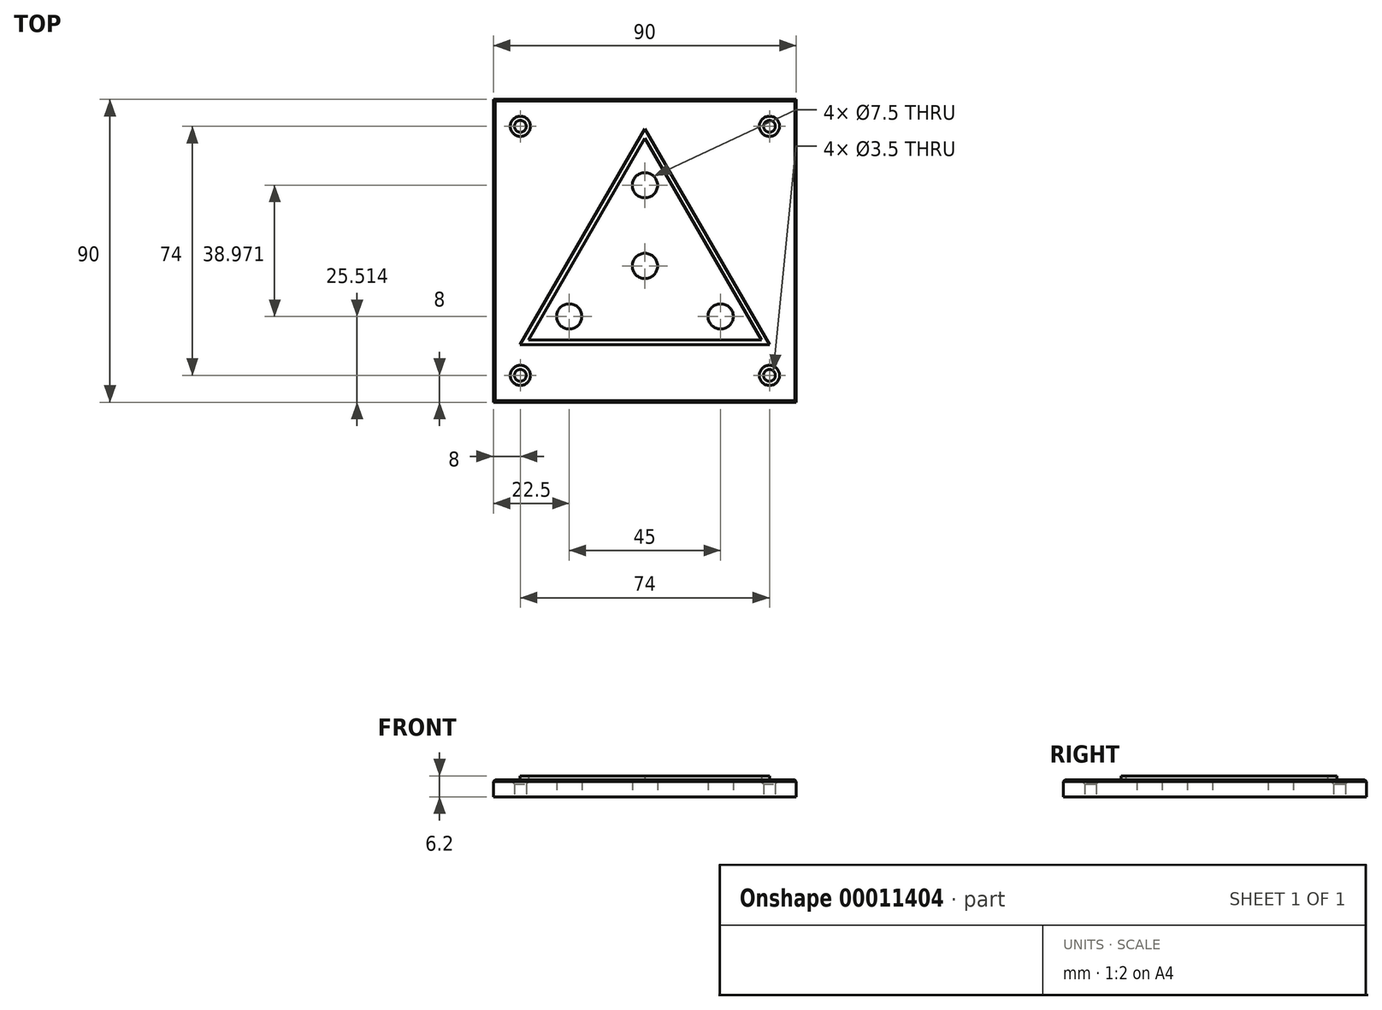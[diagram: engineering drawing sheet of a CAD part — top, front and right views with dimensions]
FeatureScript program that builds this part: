
annotation { "Feature Type Name" : "Feature", "Feature Type Description" : "" }
export const myFeature = defineFeature(function(context is Context, id is Id, definition is map)
    precondition{}
    {
        {
            var Q0;
            Q0=qCreatedBy(makeId("Top.planeOp"),FACE);
            var sketch = newSketch(context, id + "F0", { "sketchPlane" : qUnion([Q0])});
            skLineSegment(sketch, "E0.bottom", {"start": v(-45, 45) * mm, "end": v(45, 45) * mm});
            skLineSegment(sketch, "E0.top", {"start": v(-45, -45) * mm, "end": v(45, -45) * mm});
            skLineSegment(sketch, "E0.left", {"start": v(-45, 45) * mm, "end": v(-45, -45) * mm});
            skLineSegment(sketch, "E0.right", {"start": v(45, 45) * mm, "end": v(45, -45) * mm});
            skLineSegment(sketch, "E1", {"start": v(-45, -45) * mm, "end": v(45, 45) * mm, "construction": true});
            skPoint(sketch, "E2", {"position": v(0, 19.49) * mm});
            skPoint(sketch, "E3", {"position": v(-22.5, -19.49) * mm});
            skPoint(sketch, "E4", {"position": v(22.5, -19.49) * mm});
            skPoint(sketch, "E5", {"position": v(0, -4.49) * mm});
            skLineSegment(sketch, "E6", {"start": v(0, 19.49) * mm, "end": v(-22.5, -19.49) * mm, "construction": true});
            skLineSegment(sketch, "E7", {"start": v(22.5, -19.49) * mm, "end": v(-22.5, -19.49) * mm, "construction": true});
            skLineSegment(sketch, "E8", {"start": v(0, 19.49) * mm, "end": v(22.5, -19.49) * mm, "construction": true});
            skLineSegment(sketch, "E9", {"start": v(0, 19.49) * mm, "end": v(0, -19.49) * mm, "construction": true});
            skLineSegment(sketch, "E10", {"start": v(0, 19.49) * mm, "end": v(0, 45) * mm, "construction": true});
            skLineSegment(sketch, "E11", {"start": v(0, -19.49) * mm, "end": v(0, -45) * mm, "construction": true});
            skSolve(sketch);
        }
        {
            var Q0;
            Q0 = qSketchRegion(id + "F0", true);
            extrude(context, id + "F1", {"entities" : qUnion([Q0]), "depth" : 5 * mm});
        }
        {
            var Q0;
            Q0=qCreatedBy(makeId("Top.planeOp"),FACE);
            var sketch = newSketch(context, id + "F2", { "sketchPlane" : qUnion([Q0])});
            skPoint(sketch, "E12.0", {"position": v(0, 19.49) * mm});
            skPoint(sketch, "E12.1", {"position": v(-22.5, -19.49) * mm});
            skPoint(sketch, "E12.2", {"position": v(22.5, -19.49) * mm});
            skPoint(sketch, "E12.3", {"position": v(0, -4.49) * mm});
            skCircle(sketch, "E13", {"center": v(0, 19.49) * mm, "radius": 3.75 * mm});
            skCircle(sketch, "E14", {"center": v(0, -4.49) * mm, "radius": 3.75 * mm});
            skCircle(sketch, "E15", {"center": v(-22.5, -19.49) * mm, "radius": 3.75 * mm});
            skCircle(sketch, "E16", {"center": v(22.5, -19.49) * mm, "radius": 3.75 * mm});
            skSolve(sketch);
        }
        {
            var Q0;
            Q0 = qSketchRegion(id + "F2", true);
            extrude(context, id + "F3", {"entities" : qUnion([Q0]), "operationType" : NewBodyOperationType.REMOVE, "endBound" : BoundingType.THROUGH_ALL, "depth" : 1 * mm});
        }
        {
            var Q0;
            Q0=makeQuery(id+"F1.opExtrude","CAP_FACE",FACE,{"disambiguationData":[OSD([sQuery(id+"F0.wireOp",EDGE,"E0.bottom"),sQuery(id+"F0.wireOp",EDGE,"E0.top"),sQuery(id+"F0.wireOp",EDGE,"E0.left"),sQuery(id+"F0.wireOp",EDGE,"E0.right")])],"isStart":false});
            var sketch = newSketch(context, id + "F4", { "sketchPlane" : qUnion([Q0])});
            skLineSegment(sketch, "E17", {"start": v(0, 33.49) * mm, "end": v(-34.62, -26.49) * mm});
            skLineSegment(sketch, "E18", {"start": v(-34.62, -26.49) * mm, "end": v(34.62, -26.49) * mm});
            skLineSegment(sketch, "E19", {"start": v(34.62, -26.49) * mm, "end": v(0, 33.49) * mm});
            skLineSegment(sketch, "E20", {"start": v(0, 36.29) * mm, "end": v(-37.05, -27.89) * mm});
            skLineSegment(sketch, "E21", {"start": v(-37.05, -27.89) * mm, "end": v(37.05, -27.89) * mm});
            skLineSegment(sketch, "E22", {"start": v(37.05, -27.89) * mm, "end": v(0, 36.29) * mm});
            skSolve(sketch);
        }
        {
            var Q0;
            Q0 = qSketchRegion(id + "F4", true);
            extrude(context, id + "F5", {"entities" : qUnion([Q0]), "operationType" : NewBodyOperationType.ADD, "depth" : 1.2 * mm});
        }
        {
            var Q0;
            Q0=makeQuery(id+"F1.opExtrude","CAP_EDGE",EDGE,{"disambiguationData":[OSD([sQuery(id+"F0.wireOp",EDGE,"E0.left")])],"isStart":false});
            var Q1;
            Q1=makeQuery(id+"F1.opExtrude","CAP_EDGE",EDGE,{"disambiguationData":[OSD([sQuery(id+"F0.wireOp",EDGE,"E0.top")])],"isStart":false});
            var Q2;
            Q2=makeQuery(id+"F1.opExtrude","CAP_EDGE",EDGE,{"disambiguationData":[OSD([sQuery(id+"F0.wireOp",EDGE,"E0.right")])],"isStart":false});
            var Q3;
            Q3=makeQuery(id+"F1.opExtrude","CAP_EDGE",EDGE,{"disambiguationData":[OSD([sQuery(id+"F0.wireOp",EDGE,"E0.bottom")])],"isStart":false});
            chamfer(context, id + "F6", {"entities" : qUnion([Q0, Q1, Q2, Q3]), "width" : 0.5 * mm, "tangentPropagation" : true});
        }
        {
            var Q0;
            {var subQ0=sQuery(id+"F0.wireOp",EDGE,"E0.right");var subQ1=sQuery(id+"F0.wireOp",EDGE,"E0.left");var subQ2=sQuery(id+"F0.wireOp",EDGE,"E0.top");var subQ3=sQuery(id+"F0.wireOp",EDGE,"E0.bottom");Q0=makeQuery(id+"F5.boolean.opBoolean","SPLIT",FACE,{"disambiguationData":[TD([makeQuery(id+"F1.opExtrude","SWEPT_FACE",FACE,{"disambiguationData":[OSD([subQ3])]})])],"derivedFrom":makeQuery(id+"F1.opExtrude","CAP_FACE",FACE,{"disambiguationData":[OSD([subQ3,subQ2,subQ1,subQ0])],"isStart":false})});}
            var sketch = newSketch(context, id + "F7", { "sketchPlane" : qUnion([Q0])});
            skLineSegment(sketch, "E23.bottom", {"start": v(-37, 37) * mm, "end": v(37, 37) * mm, "construction": true});
            skLineSegment(sketch, "E23.top", {"start": v(-37, -37) * mm, "end": v(37, -37) * mm, "construction": true});
            skLineSegment(sketch, "E23.left", {"start": v(-37, 37) * mm, "end": v(-37, -37) * mm, "construction": true});
            skLineSegment(sketch, "E23.right", {"start": v(37, 37) * mm, "end": v(37, -37) * mm, "construction": true});
            skLineSegment(sketch, "E24", {"start": v(-37, -37) * mm, "end": v(37, 37) * mm, "construction": true});
            skPoint(sketch, "E25", {"position": v(-37, 37) * mm});
            skPoint(sketch, "E26", {"position": v(37, 37) * mm});
            skPoint(sketch, "E27", {"position": v(37, -37) * mm});
            skPoint(sketch, "E28", {"position": v(-37, -37) * mm});
            skSolve(sketch);
        }
        {
            var Q0;
            Q0=sQuery(id+"F7.wireOp",VERTEX,"E25");
            var Q1;
            Q1=sQuery(id+"F7.wireOp",VERTEX,"E26");
            var Q2;
            Q2=sQuery(id+"F7.wireOp",VERTEX,"E27");
            var Q3;
            Q3=sQuery(id+"F7.wireOp",VERTEX,"E28");
            var Q4;
            Q4=makeQuery(id+"F1.opExtrude","SWEPT_BODY",BODY,{"disambiguationData":[OSD([sQuery(id+"F0.wireOp",EDGE,"E0.bottom"),sQuery(id+"F0.wireOp",EDGE,"E0.top"),sQuery(id+"F0.wireOp",EDGE,"E0.left"),sQuery(id+"F0.wireOp",EDGE,"E0.right")])]});
            hole(context, id + "F8", {"style" : HoleStyle.C_SINK, "holeDiameter" : 3.5 * mm, "cSinkDiameter" : 6 * mm, "endStyle" : HoleEndStyle.THROUGH, "locations" : qUnion([Q0, Q1, Q2, Q3]), "scope" : qUnion([Q4]), "cSinkAngle" : 90 * degree});
        }
    });
